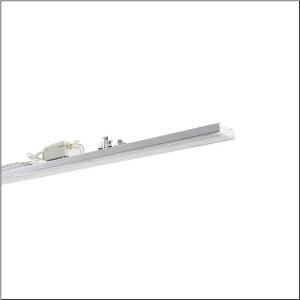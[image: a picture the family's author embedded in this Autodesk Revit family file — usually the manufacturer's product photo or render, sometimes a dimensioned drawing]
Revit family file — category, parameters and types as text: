
# Revit family: licross_21_recessed_mo_52te12dn4axg
name_source: partatom
category: Lighting Fixtures
units: mm (PartAtom-declared; Revit-internal decimal feet)

## family parameters
Cut with Voids When Loaded = No
Host = Face
Light Source = No
Part Type = Normal
Room Calculation Point = No
Round Connector Dimension = Use Diameter
Shared = No

## types (1)
- --- (1 x LED, 10280 lm, 58 W, 4000K)
    Apparent Load = 58 VA
    CIE Flux Codes = 72 92 99 100 100
    Color Rendering = 80
    Color Temperature = 4000K
    Default Elevation = 1800 mm
    Description = Licross 21 Recessed MO, luminaire insert, of sheet steel, galvanised, coil coated, white, length: 1.500mm, width: 66mm, height: 67mm, LED rated luminous flux: 10.280lm, light colour: 840, SDCM (Standard Deviation of Colour Matching)MacAdam ≤ 3 SDCM (initial), control gear: DALI 2, with plug, 5-pole, with phase selection, mains connection: 220..240V, AC, 50/60Hz, rated input power: 58W, internal wiring halogen-free, primary optical cover: cover, of PMMA, light emission: direct distribution, primary light characteristic: symmetric, protection rating (complete): IP54, insulation class (complete): insulation class I (protective earthing), certification: CE, ENEC, VDE, UKCA, protection symbol: D if used in an environment with non-conductive dust loads with corresponding accessories, impact resistance: IK06, permissible ambient temperature for indoor applications: -25..+35°C, corresponds to IFS (International Featured Standards) requirements for safety and quality in the food industry, reducing of maximum allowable ambient temperature of 5°C with ceiling mounting, LABS conformity tested according to VDMA 24364:2018-05, The light source and the operating device comply with the requirements of the Ecodesign Regulation (EU) 2019/2020 and are replaceable in accordance with this regulation, packaging unit: 1 piece
    Height = 58 mm
    Lamp = 1 x LED
    Lamp Light Flux = 10280 lm
    Lamp Power = 58 W
    Lamp count = 1
    Length = 1500 mm
    Luminous efficacy = 177 lm/W
    Manufacturer = Siteco
    ModVariant = No
    Model = 52TE12DN4AXG
    Mounting Place = Ceiling
    Mounting Type = Pendant
    Number of Poles = 1
    OnlyDefault = Yes
    Power Factor = 1
    Product Name = Licross 21 Recessed MO
    Product group = luminaire insert | ceiling pendant
    ProductGroupID = 901
    Protection Class = Protection class I
    Protection Degree = IP 54
    RLX_Detail_Level = 1
    RLX_Emergency_Light_Flux = 0 lm
    RLX_Emergency_Type = 0
    RLX_Emergency_Type_DB = No
    RlxData = <blob elided: 24933 chars, md5=01e1f126>
    Socket = socket
    Standby Power = 0 W
    System Light Flux = 10280 lm
    System Power = 58 W
    Type Comments = factory setting: luminous flux: 100 % | dim-lin: 254 | 390 mA
    Type Image = l_1296930.jpg
    URL = http://relux.com
    VarID = @adj_127855
    Voltage = 0 V
    Weight = 0.00 kg
    Width = 66 mm

## geometry (parser evidence)
native form markers: Blend x4, Sweep x11
no freeform markers — native parametric forms only
